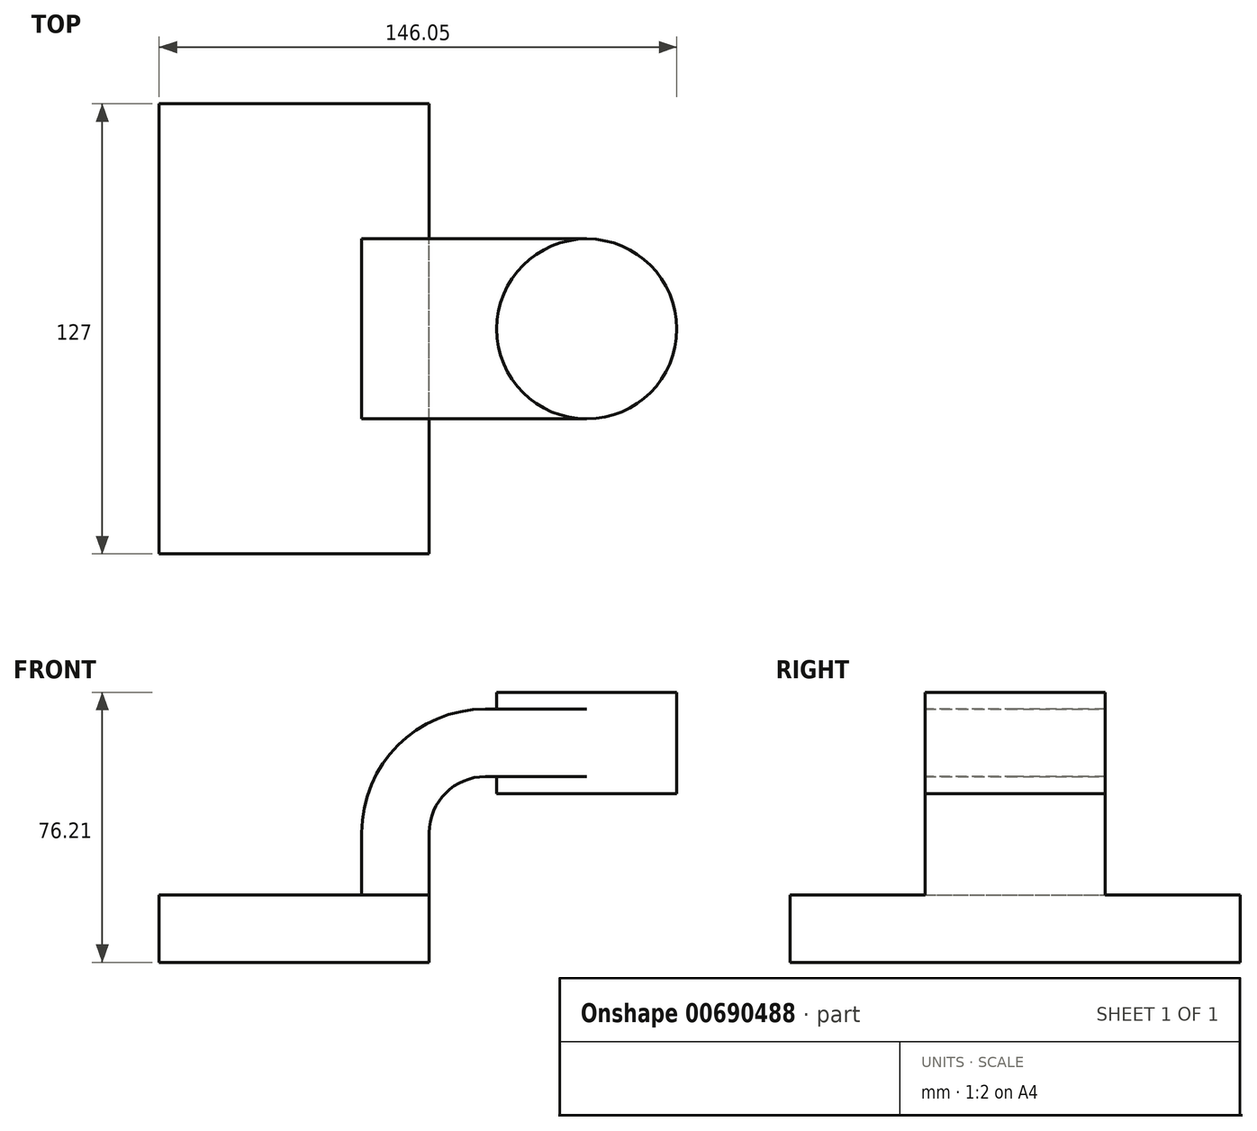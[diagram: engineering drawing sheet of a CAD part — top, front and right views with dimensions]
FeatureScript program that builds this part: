
annotation { "Feature Type Name" : "Feature", "Feature Type Description" : "" }
export const myFeature = defineFeature(function(context is Context, id is Id, definition is map)
    precondition{}
    {
        {
            var Q0;
            Q0=qCreatedBy(makeId("Front.planeOp"),FACE);
            var sketch = newSketch(context, id + "F0", { "sketchPlane" : qUnion([Q0])});
            skLineSegment(sketch, "E0.bottom", {"start": v(38.1, -9.52) * mm, "end": v(-38.1, -9.52) * mm});
            skLineSegment(sketch, "E0.top", {"start": v(38.1, 9.53) * mm, "end": v(-38.1, 9.53) * mm});
            skLineSegment(sketch, "E0.left", {"start": v(38.1, -9.52) * mm, "end": v(38.1, 9.53) * mm});
            skLineSegment(sketch, "E0.right", {"start": v(-38.1, -9.52) * mm, "end": v(-38.1, 9.53) * mm});
            skPoint(sketch, "E0.middle", {"position": v(0, 0) * mm});
            skLineSegment(sketch, "E1.bottom", {"start": v(107.95, 38.1) * mm, "end": v(57.15, 38.1) * mm});
            skLineSegment(sketch, "E1.top", {"start": v(107.95, 66.68) * mm, "end": v(57.15, 66.68) * mm});
            skLineSegment(sketch, "E1.left", {"start": v(107.95, 38.1) * mm, "end": v(107.95, 66.68) * mm});
            skLineSegment(sketch, "E1.right", {"start": v(57.15, 38.1) * mm, "end": v(57.15, 66.68) * mm});
            skPoint(sketch, "E1.middle", {"position": v(82.55, 52.39) * mm});
            skLineSegment(sketch, "E2", {"start": v(38.1, 9.53) * mm, "end": v(38.1, 27) * mm});
            skArc(sketch, "E3", {"start": v(38.1, 27) * mm, "mid": v(42.75, 38.23) * mm, "end": v(53.97, 42.88) * mm});
            skArc(sketch, "E4.1", {"start": v(19.05, 27) * mm, "mid": v(29.28, 51.7) * mm, "end": v(53.97, 61.93) * mm});
            skLineSegment(sketch, "E4.2", {"start": v(19.05, 9.53) * mm, "end": v(19.05, 27) * mm});
            skLineSegment(sketch, "E5", {"start": v(53.97, 42.88) * mm, "end": v(82.55, 42.88) * mm});
            skPoint(sketch, "E5.endSnap0", {"position": v(82.55, 38.1) * mm});
            skLineSegment(sketch, "E6", {"start": v(82.55, 42.88) * mm, "end": v(82.55, 61.93) * mm});
            skLineSegment(sketch, "E7", {"start": v(53.97, 61.93) * mm, "end": v(82.55, 61.93) * mm});
            skLineSegment(sketch, "E8", {"start": v(82.55, 38.1) * mm, "end": v(82.55, 66.68) * mm});
            skFitSpline(sketch, "E9", {"points": [v(-38.1, 9.53) * mm, v(53.97, 61.93) * mm], "startDerivative": vector(0, 61.9) * mm, "endDerivative": vector(161.92, 0) * mm});
            skSolve(sketch);
        }
        {
            var Q0;
            Q0=makeQuery(id+"F0.imprint","IMPRINT",FACE,{"disambiguationData":[TD([[makeQuery(id+"F0.imprint","IMPRINT",EDGE,{"derivedFrom":sQuery(id+"F0.wireOp",EDGE,"E0.bottom")}),-1.0]])]});
            extrude(context, id + "F1", {"entities" : qUnion([Q0]), "endBound" : BoundingType.SYMMETRIC, "depth" : 127 * mm, "offsetDistance" : 25.4 * mm});
        }
        {
            var Q0;
            {var subQ1=sQuery(id+"F0.wireOp",EDGE,"E2");Q0=makeQuery(id+"F0.imprint","IMPRINT",FACE,{"disambiguationData":[TD([[makeQuery(id+"F0.imprint","IMPRINT",EDGE,{"derivedFrom":subQ1}),1.0]])]});}
            var Q1;
            {var subQ0=sQuery(id+"F0.wireOp",EDGE,"E5");var subQ1=sQuery(id+"F0.wireOp",EDGE,"E1.right");var subQ2=makeQuery(id+"F0.imprint","INTERSECT",VERTEX,{"derivedFrom":[subQ1,subQ0]});Q1=makeQuery(id+"F0.imprint","IMPRINT",FACE,{"disambiguationData":[TD([[makeQuery(id+"F0.imprint","IMPRINT",EDGE,{"disambiguationData":[TD([[subQ2,-1.0]])],"derivedFrom":subQ1}),-1.0]])]});}
            extrude(context, id + "F2", {"entities" : qUnion([Q0, Q1]), "operationType" : NewBodyOperationType.ADD, "endBound" : BoundingType.SYMMETRIC, "depth" : 50.8 * mm, "offsetDistance" : 25.4 * mm});
        }
        {
            var Q0;
            Q0=makeQuery(id+"F0.imprint","IMPRINT",FACE,{"disambiguationData":[TD([[makeQuery(id+"F0.imprint","IMPRINT",EDGE,{"derivedFrom":sQuery(id+"F0.wireOp",EDGE,"E4.1")}),1.0]])]});
            extrude(context, id + "F3", {"entities" : qUnion([Q0]), "operationType" : NewBodyOperationType.ADD, "endBound" : BoundingType.SYMMETRIC, "depth" : 15.88 * mm, "offsetDistance" : 25.4 * mm});
        }
        {
            var Q0;
            {var subQ4=sQuery(id+"F0.wireOp",EDGE,"E1.left");Q0=makeQuery(id+"F0.imprint","IMPRINT",FACE,{"disambiguationData":[TD([[makeQuery(id+"F0.imprint","IMPRINT",EDGE,{"derivedFrom":subQ4}),1.0]])]});}
            var Q1;
            Q1=sQuery(id+"F0.wireOp",EDGE,"E8");
            revolve(context, id + "F4", {"operationType" : NewBodyOperationType.ADD, "entities" : qUnion([Q0]), "axis" : qUnion([Q1]), "revolveType" : RevolveType.FULL});
        }
    });
